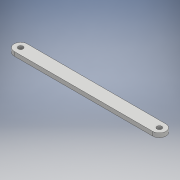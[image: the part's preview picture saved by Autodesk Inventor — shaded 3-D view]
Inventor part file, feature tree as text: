
AUTODESK INVENTOR PART (.ipt)
format: ipt  version: 2018 (Build 220112000, 112)  size: 103,936 bytes
history: native  units: mm
features: extrude x1, sketch x1
ambient origin geometry x8: Origin, YZ Plane, XZ Plane, XY Plane, X Axis, Y Axis, Z Axis, Center Point
bodies: Solid1 (feature_tree)
feature tree (2):
  extrude  "Extrusion1"  Depth=3.0mm
  sketch  "Sketch1"  dims[d0=3.556mm d1=3.556mm d2=101.6mm d3=3.0mm d4=3.0mm d5=3.0mm d6=0.0mm]
